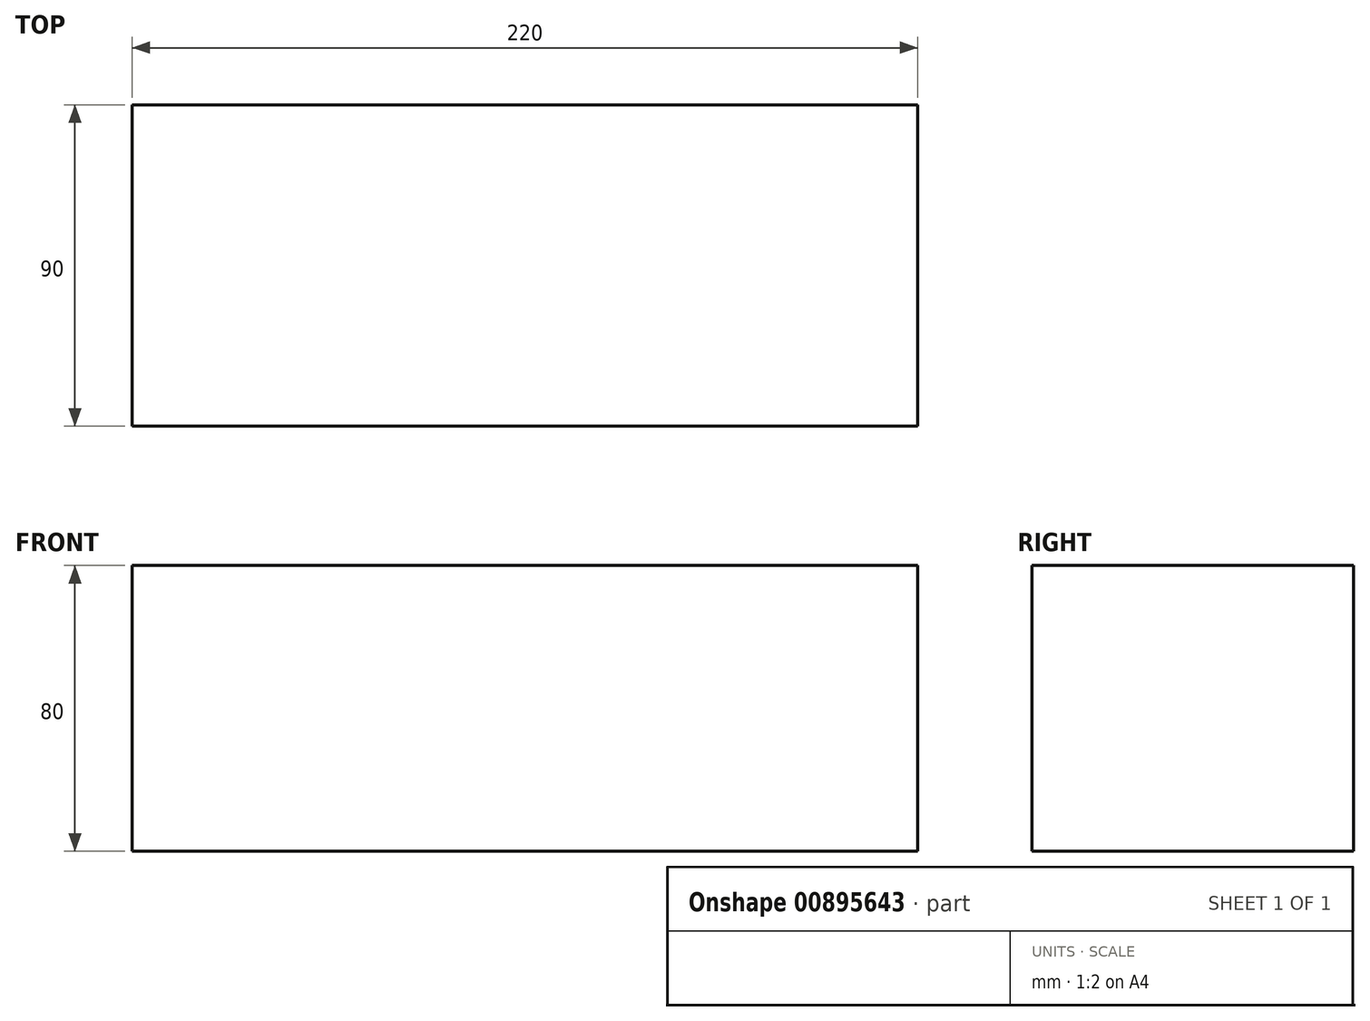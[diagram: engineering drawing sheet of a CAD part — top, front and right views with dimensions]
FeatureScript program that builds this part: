
annotation { "Feature Type Name" : "Feature", "Feature Type Description" : "" }
export const myFeature = defineFeature(function(context is Context, id is Id, definition is map)
    precondition{}
    {
        {
            var Q0;
            Q0=qCreatedBy(makeId("Top.planeOp"),FACE);
            var sketch = newSketch(context, id + "F0", { "sketchPlane" : qUnion([Q0])});
            skLineSegment(sketch, "E0.bottom", {"start": v(110, -45) * mm, "end": v(-110, -45) * mm});
            skLineSegment(sketch, "E0.top", {"start": v(110, 45) * mm, "end": v(-110, 45) * mm});
            skLineSegment(sketch, "E0.left", {"start": v(110, -45) * mm, "end": v(110, 45) * mm});
            skLineSegment(sketch, "E0.right", {"start": v(-110, -45) * mm, "end": v(-110, 45) * mm});
            skPoint(sketch, "E0.middle", {"position": v(0, 0) * mm});
            skSolve(sketch);
        }
        {
            var Q0;
            Q0=makeQuery(id+"F0.imprint","IMPRINT",FACE,{"disambiguationData":[TD([[makeQuery(id+"F0.imprint","IMPRINT",EDGE,{"derivedFrom":sQuery(id+"F0.wireOp",EDGE,"E0.bottom")}),-1.0]])]});
            extrude(context, id + "F1", {"entities" : qUnion([Q0]), "depth" : 80 * mm, "offsetDistance" : 25 * mm});
        }
    });
